FREECAD ASSEMBLY — COMPONENT RECIPES ("clamp1")

This assembly document has 7 components, labeled P0..P6 below (a component is one placed body or linked part). 4 of them carry a construction recipe — the FreeCAD feature program that regenerates the part from scratch, quoted from this document or its linked companion documents; the rest are supplied as boundary geometry only. No exploded tour is included for this assembly.
COMPONENT P0 — geometry summary ("Body"; no construction recipe available for this part):
  bounding box: 60.0 x 20.2 x 10.0 mm
  tessellated surface: 1,496 triangles
  volume: 2227 mm^3 (18% of its bounding box)
  symmetry: 2-fold rotationally symmetric about the y axis; mirror-symmetric across its x mid-plane, z mid-plane
COMPONENT P1 — geometry summary ("Body001"; no construction recipe available for this part):
  bounding box: 60.0 x 20.2 x 10.0 mm
  tessellated surface: 1,496 triangles
  volume: 2227 mm^3 (18% of its bounding box)
  symmetry: 2-fold rotationally symmetric about the y axis; mirror-symmetric across its x mid-plane, z mid-plane
COMPONENT P2 — geometry summary ("Extrude001"; no construction recipe available for this part):
  bounding box: 80.0 x 12.0 x 3.0 mm
  tessellated surface: 520 triangles
  volume: 2821 mm^3 (98% of its bounding box)
  symmetry: 2-fold rotationally symmetric about the z axis; mirror-symmetric across its x mid-plane, y mid-plane
COMPONENT P3 — recipe-attached ("M5-Nut", a linked part whose construction recipe lives in a companion FreeCAD document of the same project; that document's serialized recipe follows).
Construction recipe (the companion document, serialized — sketch geometry with constraints, then the solid features built on it; lengths are millimeters unless a unit is written):

FCSTD DOCUMENT  (FreeCAD 1.0R39319 (Git))
Label: nut
License: All rights reserved
LicenseURL: https://en.wikipedia.org/wiki/All_rights_reserved
objects: Part::FeaturePython×1
note: 1 computed .brp shape members not serialized (recipe doc carries the construction recipe); baked Part::Feature solids carry a one-line shape summary decoded from their .brp

FEATURE [Part::FeaturePython] Nut  label="M5-Nut"  # WARN: FeaturePython — macro-defined, semantics opaque (R4)
  Diameter = 7
  Invert = false
  LeftHanded = false
  MatchOuter = false
  OffsetAngle = 0
  Thread = true
  Type = 31
COMPONENT P4 — same part as P3; its construction recipe is shown at P3.
COMPONENT P5 — recipe-attached ("M5x12-Screw", a linked part whose construction recipe lives in a companion FreeCAD document of the same project; that document's serialized recipe follows).
Construction recipe (the companion document, serialized — sketch geometry with constraints, then the solid features built on it; lengths are millimeters unless a unit is written):

FCSTD DOCUMENT  (FreeCAD 1.0R39319 (Git))
Label: screw
License: All rights reserved
LicenseURL: https://en.wikipedia.org/wiki/All_rights_reserved
objects: Part::FeaturePython×1
note: 1 computed .brp shape members not serialized (recipe doc carries the construction recipe); baked Part::Feature solids carry a one-line shape summary decoded from their .brp

FEATURE [Part::FeaturePython] Screw  label="M5x12-Screw"  # WARN: FeaturePython — macro-defined, semantics opaque (R4)
  Diameter = 7
  Invert = false
  LeftHanded = false
  Length = 3
  LengthCustom = 12
  MatchOuter = false
  OffsetAngle = 0
  Thread = true
  Type = 54
COMPONENT P6 — same part as P5; its construction recipe is shown at P5.
PROVENANCE & LICENSES
A FreeCAD (.FCStd) document from a public repository crawl; recipes are the document's own serialized feature recipes (and, for linked parts, companion documents' recipes).
License: as declared in the source repository (recorded in the dataset sidecar).
